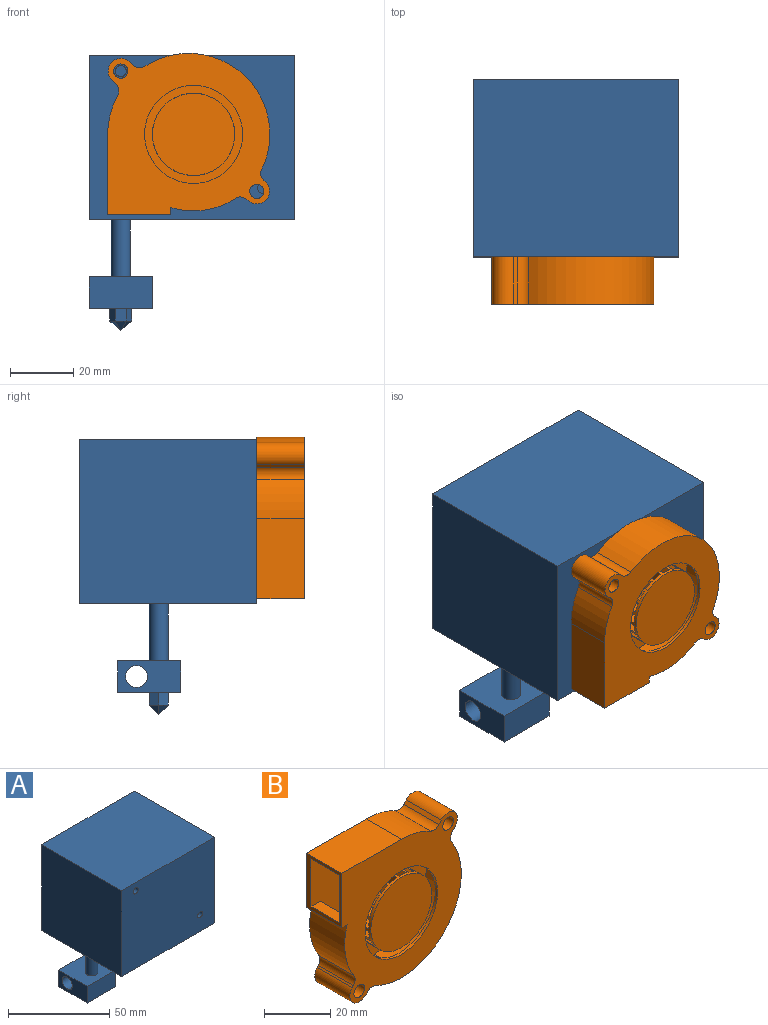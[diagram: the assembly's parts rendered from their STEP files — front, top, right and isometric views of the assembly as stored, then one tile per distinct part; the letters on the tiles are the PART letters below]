
ASSEMBLY  parts=2 mates=1
PART A: 30 faces, bbox 65x56x87 mm
  f0: cylinder r=3mm len=18mm, axis (0,0,-1), area 339.3mm2, adj f5,f25
  f1: plane 20x10mm, normal (1,0,0), area 161.5mm2, adj f2,f4,f5,f6,f7
  f2: plane 20x10mm, normal (0,1,0), area 200mm2, adj f1,f3,f5,f6
  f3: plane 20x10mm, normal (-1,0,0), area 161.5mm2, adj f2,f4,f5,f6,f7
  f4: plane 20x10mm, normal (0,-1,0), area 200mm2, adj f1,f3,f5,f6
  f5: plane 20x20mm, normal (0,0,1), area 371.7mm2, adj f0,f1,f2,f3,f4
  f6: plane 20x20mm, normal (0,0,-1), area 368.8mm2, adj f1,f2,f3,f4,f8,f9,f10,f11
  f7: cylinder r=3.5mm len=20mm, axis (1,0,0), area 439.8mm2, adj f1,f3
  f8: plane 4x3.46mm, normal (0,1,0), area 13.9mm2, adj f6,f9,f13,f14
  f9: plane 4x3mm, normal (0.87,0.5,0), area 13.9mm2, adj f6,f8,f10,f15
  f10: plane 4x3mm, normal (0.87,-0.5,0), area 13.9mm2, adj f6,f9,f11,f16
  f11: plane 4x3.46mm, normal (0,-1,0), area 13.9mm2, adj f6,f10,f12,f17
  f12: plane 4x3mm, normal (-0.87,-0.5,0), area 13.9mm2, adj f6,f11,f13,f18
  f13: plane 4x3mm, normal (-0.87,0.5,0), area 13.9mm2, adj f6,f8,f12,f19
  f14: plane 3.46x3mm, normal (0,0.71,-0.71), area 7.3mm2, adj f8,f15,f19
  f15: plane 3.46x3mm, normal (0.61,0.35,-0.71), area 7.3mm2, adj f9,f14,f16
  f16: plane 3.46x3mm, normal (0.61,-0.35,-0.71), area 7.3mm2, adj f10,f15,f17
  f17: plane 3.46x3mm, normal (0,-0.71,-0.71), area 7.3mm2, adj f11,f16,f18
  f18: plane 3.46x3mm, normal (-0.61,-0.35,-0.71), area 7.3mm2, adj f12,f17,f19
  f19: plane 3.46x3mm, normal (-0.61,0.35,-0.71), area 7.3mm2, adj f13,f14,f18
  f20: plane 56x52mm, normal (-1,0,0), area 2912mm2, adj f21,f23,f24,f25
  f21: plane 65x52mm, normal (0,-1,0), area 3360.8mm2, adj f20,f22,f24,f25,f26,f28
  f22: plane 56x52mm, normal (1,0,0), area 2912mm2, adj f21,f23,f24,f25
  f23: plane 65x52mm, normal (0,1,0), area 3380mm2, adj f20,f22,f24,f25
  f24: plane 65x56mm, normal (0,0,1), area 3640mm2, adj f20,f21,f22,f23
  f25: plane 65x56mm, normal (0,0,-1), area 3611.7mm2, adj f0,f20,f21,f22,f23
  f26: cylinder r=1.75mm len=25mm, axis (0,-1,0), area 274.9mm2, adj f21,f27
  f27: plane 3.5x3.5mm, normal (0,-1,0), area 9.6mm2, adj f26
  f28: cylinder r=1.75mm len=25mm, axis (0,-1,0), area 274.9mm2, adj f21,f29
  f29: plane 3.5x3.5mm, normal (0,-1,0), area 9.6mm2, adj f28
PART B: 132 faces, bbox 51x15x51.3 mm
  f0: plane 51.3x51mm, normal (0,-1,0), area 1490mm2, adj f1,f3,f4,f5,f6,f7,f8,f9
  f1: cylinder r=2.25mm len=15mm, axis (0,-1,0), area 212.1mm2, adj f0,f2
  f2: plane 51.3x51mm, normal (0,1,0), area 2244.8mm2, adj f1,f3,f4,f5,f6,f7,f8,f9
  f3: plane 20x15mm, normal (-1,0,0), area 85.3mm2, adj f0,f2,f14,f15,f16,f17,f25,f26
  f4: cylinder r=25.65mm len=15mm, axis (0,-1,0), area 194.4mm2, adj f0,f2,f15,f21
  f5: plane 15x1.06mm, normal (-0.75,0,0.66), area 21.3mm2, adj f0,f2,f6,f21
  f6: cylinder r=4mm len=15mm, axis (0,-1,0), area 188.5mm2, adj f0,f2,f5,f7
  f7: plane 15x1.36mm, normal (0.75,0,-0.66), area 27.2mm2, adj f0,f2,f6,f20
  f8: cylinder r=25.65mm len=39.47mm, axis (0,-1,0), area 798.2mm2, adj f0,f2,f9,f20
  f9: cylinder r=24.2mm len=15mm, axis (0,-1,0), area 196.5mm2, adj f0,f2,f8,f18
  f10: plane 15x0.45mm, normal (0.75,0,-0.66), area 9.1mm2, adj f0,f2,f11,f18
  f11: cylinder r=4mm len=15mm, axis (0,-1,0), area 188.5mm2, adj f0,f2,f10,f12
  f12: plane 15x0.54mm, normal (-0.75,0,0.66), area 10.8mm2, adj f0,f2,f11,f19
  f13: cylinder r=24.2mm len=20.34mm, axis (0,-1,0), area 318.2mm2, adj f0,f2,f14,f19
  f14: plane 15x2.27mm, normal (0,0,-1), area 34mm2, adj f0,f2,f3,f13
  f15: plane 25.35x15mm, normal (0,0,1), area 380.2mm2, adj f0,f2,f3,f4
  f16: plane 49.8x48.9mm, normal (0,-1,0), area 1831.8mm2, adj f3,f23,f24,f25,f26,f31
  f17: plane 49.8x48.9mm, normal (0,1,0), area 1231mm2, adj f3,f22,f23,f24,f25,f26
  f18: cylinder r=3mm len=15mm, axis (0,-1,0), area 59.3mm2, adj f0,f2,f9,f10
  f19: cylinder r=3mm len=15mm, axis (0,-1,0), area 58.6mm2, adj f0,f2,f12,f13
  f20: cylinder r=3mm len=15mm, axis (0,-1,0), area 58.3mm2, adj f0,f2,f7,f8
  f21: cylinder r=3mm len=15mm, axis (0,-1,0), area 60.8mm2, adj f0,f2,f4,f5
  f22: cylinder r=15.5mm len=31mm, axis (0,-1,0), area 97.4mm2, adj f0,f17
  f23: cylinder r=24.45mm len=48.84mm, axis (0,-1,0), area 916.9mm2, adj f16,f17,f24,f26
  f24: cylinder r=23mm len=31.3mm, axis (0,-1,0), area 564mm2, adj f16,f17,f23,f25
  f25: plane 12.2x3.95mm, normal (0,0,1), area 48.2mm2, adj f3,f16,f17,f24
  f26: plane 25.35x12.2mm, normal (0,0,-1), area 309.3mm2, adj f3,f16,f17,f23
  f27: cylinder r=2.25mm len=15mm, axis (0,-1,0), area 212.1mm2, adj f0,f2
  f28: cylinder r=13mm len=26mm, axis (0,-1,0), area 383.6mm2, adj f29,f30,f40,f41,f42,f43,f44,f45
  f29: plane 26x26mm, normal (0,-1,0), area 530.9mm2, adj f28
  f30: plane 6.3x3.02mm, normal (0,1,0), area 12.8mm2, adj f28,f37,f49,f50
  f31: cylinder r=7mm len=14mm, axis (0,-1,0), area 8.8mm2, adj f16,f94
  f32: cylinder r=7mm len=11mm, axis (0,-1,0), area 13.2mm2, adj f40,f79,f118,f123
  f33: cylinder r=7mm len=11mm, axis (0,-1,0), area 13.2mm2, adj f41,f42,f117,f124
  f34: cylinder r=7mm len=11mm, axis (0,-1,0), area 13.2mm2, adj f43,f44,f116,f125
  f35: cylinder r=7mm len=11mm, axis (0,-1,0), area 13.2mm2, adj f45,f46,f115,f126
  f36: cylinder r=7mm len=11mm, axis (0,-1,0), area 13.2mm2, adj f47,f48,f96,f113
  f37: cylinder r=7mm len=11mm, axis (0,-1,0), area 13.2mm2, adj f30,f49,f50,f114
  f38: cylinder r=7mm len=11mm, axis (0,-1,0), area 13.2mm2, adj f51,f52,f106,f128
  f39: cylinder r=7mm len=11mm, axis (0,-1,0), area 13.2mm2, adj f53,f54,f107,f129
  f40: plane 11x5.71mm, normal (0.95,0,0.31), area 66mm2, adj f28,f32,f118,f123
  f41: plane 11x5.74mm, normal (-0.95,0,-0.31), area 66.4mm2, adj f28,f33,f117,f124
  f42: plane 11x4.85mm, normal (0.81,0,0.59), area 66mm2, adj f28,f33,f117,f124
  f43: plane 11x4.88mm, normal (-0.81,0,-0.59), area 66.4mm2, adj f28,f34,f116,f125
  f44: plane 11x4.85mm, normal (0.59,0,0.81), area 66mm2, adj f28,f34,f116,f125
  f45: plane 11x4.88mm, normal (-0.59,0,-0.81), area 66.4mm2, adj f28,f35,f115,f126
  f46: plane 11x5.71mm, normal (0.31,0,0.95), area 66mm2, adj f28,f35,f115,f126
  f47: plane 11x5.74mm, normal (-0.31,0,-0.95), area 66.4mm2, adj f28,f36,f96,f113
  f48: plane 11x6mm, normal (0,0,1), area 66mm2, adj f28,f36,f96,f113
  f49: plane 11x6.03mm, normal (0,0,-1), area 66.4mm2, adj f28,f30,f37,f114
  f50: plane 11x5.71mm, normal (-0.31,0,0.95), area 66mm2, adj f28,f30,f37,f114
  f51: plane 11x5.74mm, normal (0.31,0,-0.95), area 66.4mm2, adj f28,f38,f106,f128
  f52: plane 11x4.85mm, normal (-0.59,0,0.81), area 66mm2, adj f28,f38,f106,f128
  f53: plane 11x4.88mm, normal (0.59,0,-0.81), area 66.4mm2, adj f28,f39,f107,f129
  f54: plane 11x4.85mm, normal (-0.81,0,0.59), area 66mm2, adj f28,f39,f107,f129
  f55: plane 11x4.88mm, normal (0.81,0,-0.59), area 66.4mm2, adj f28,f105,f108,f130
  f56: plane 11x5.71mm, normal (-0.95,0,0.31), area 66mm2, adj f28,f105,f108,f130
  f57: plane 11x5.74mm, normal (0.95,0,-0.31), area 66.4mm2, adj f28,f104,f109,f131
  f58: plane 11x6mm, normal (-1,0,0), area 66mm2, adj f28,f104,f109,f131
  f59: plane 11x6.03mm, normal (1,0,0), area 66.4mm2, adj f28,f100,f103,f110
  f60: plane 11x5.71mm, normal (-0.95,0,-0.31), area 66mm2, adj f28,f100,f103,f110
  f61: plane 11x5.74mm, normal (0.95,0,0.31), area 66.4mm2, adj f28,f99,f101,f111
  f62: plane 11x4.85mm, normal (-0.81,0,-0.59), area 66mm2, adj f28,f99,f101,f111
  f63: plane 11x4.88mm, normal (0.81,0,0.59), area 66.4mm2, adj f28,f98,f102,f112
  f64: plane 11x4.85mm, normal (-0.59,0,-0.81), area 66mm2, adj f28,f98,f102,f112
  f65: plane 11x4.88mm, normal (0.59,0,0.81), area 66.4mm2, adj f28,f86,f88,f97
  f66: plane 11x5.71mm, normal (-0.31,0,-0.95), area 66mm2, adj f28,f86,f88,f97
  f67: plane 11x5.74mm, normal (0.31,0,0.95), area 66.4mm2, adj f28,f85,f87,f95
  f68: plane 11x6mm, normal (0,0,-1), area 66mm2, adj f28,f85,f87,f95
  f69: plane 11x6.03mm, normal (0,0,1), area 66.4mm2, adj f28,f84,f89,f93
  f70: plane 11x5.71mm, normal (0.31,0,-0.95), area 66mm2, adj f28,f84,f89,f93
  f71: plane 11x5.74mm, normal (-0.31,0,0.95), area 66.4mm2, adj f28,f83,f90,f91
  f72: plane 11x4.85mm, normal (0.59,0,-0.81), area 66mm2, adj f28,f83,f90,f91
  f73: plane 11x4.88mm, normal (-0.59,0,0.81), area 66.4mm2, adj f28,f82,f92,f127
  f74: plane 11x4.85mm, normal (0.81,0,-0.59), area 66mm2, adj f28,f82,f92,f127
  f75: plane 11x4.88mm, normal (-0.81,0,0.59), area 66.4mm2, adj f28,f81,f120,f122
  f76: plane 11x5.71mm, normal (0.95,0,-0.31), area 66mm2, adj f28,f81,f120,f122
  f77: plane 11x5.74mm, normal (-0.95,0,0.31), area 66.4mm2, adj f28,f80,f119,f121
  f78: plane 11x6mm, normal (1,0,0), area 66mm2, adj f28,f80,f119,f121
  f79: plane 11x6.03mm, normal (-1,0,0), area 66.4mm2, adj f28,f32,f118,f123
  f80: cylinder r=7mm len=11mm, axis (0,-1,0), area 13.2mm2, adj f77,f78,f119,f121
  f81: cylinder r=7mm len=11mm, axis (0,-1,0), area 13.2mm2, adj f75,f76,f120,f122
  f82: cylinder r=7mm len=11mm, axis (0,-1,0), area 13.2mm2, adj f73,f74,f92,f127
  f83: cylinder r=7mm len=11mm, axis (0,-1,0), area 13.2mm2, adj f71,f72,f90,f91
  f84: cylinder r=7mm len=11mm, axis (0,-1,0), area 13.2mm2, adj f69,f70,f89,f93
  f85: cylinder r=7mm len=11mm, axis (0,-1,0), area 13.2mm2, adj f67,f68,f87,f95
  f86: cylinder r=7mm len=11mm, axis (0,-1,0), area 13.2mm2, adj f65,f66,f88,f97
  f87: plane 6.1x3.05mm, normal (0,1,0), area 12.8mm2, adj f28,f67,f68,f85
  f88: plane 6.17x4.65mm, normal (0,1,0), area 12.8mm2, adj f28,f65,f66,f86
  f89: plane 6.3x3.02mm, normal (0,1,0), area 12.8mm2, adj f28,f69,f70,f84
  f90: plane 6.36x4.55mm, normal (0,1,0), area 12.8mm2, adj f28,f71,f72,f83
  f91: plane 6.36x4.55mm, normal (0,-1,0), area 12.8mm2, adj f28,f71,f72,f83
  f92: plane 5.78x5.64mm, normal (0,-1,0), area 12.8mm2, adj f28,f73,f74,f82
  f93: plane 6.3x3.02mm, normal (0,-1,0), area 12.8mm2, adj f28,f69,f70,f84
  f94: plane 26x26mm, normal (0,1,0), area 377mm2, adj f28,f31
  f95: plane 6.1x3.05mm, normal (0,-1,0), area 12.8mm2, adj f28,f67,f68,f85
  f96: plane 6.1x3.05mm, normal (0,1,0), area 12.8mm2, adj f28,f36,f47,f48
  f97: plane 6.17x4.65mm, normal (0,-1,0), area 12.8mm2, adj f28,f65,f66,f86
  f98: plane 5.78x5.64mm, normal (0,-1,0), area 12.8mm2, adj f28,f63,f64,f102
  f99: plane 6.36x4.55mm, normal (0,-1,0), area 12.8mm2, adj f28,f61,f62,f101
  f100: plane 6.3x3.02mm, normal (0,-1,0), area 12.8mm2, adj f28,f59,f60,f103
  f101: cylinder r=7mm len=11mm, axis (0,-1,0), area 13.2mm2, adj f61,f62,f99,f111
  f102: cylinder r=7mm len=11mm, axis (0,-1,0), area 13.2mm2, adj f63,f64,f98,f112
  f103: cylinder r=7mm len=11mm, axis (0,-1,0), area 13.2mm2, adj f59,f60,f100,f110
  f104: cylinder r=7mm len=11mm, axis (0,-1,0), area 13.2mm2, adj f57,f58,f109,f131
  f105: cylinder r=7mm len=11mm, axis (0,-1,0), area 13.2mm2, adj f55,f56,f108,f130
  f106: plane 6.36x4.55mm, normal (0,1,0), area 12.8mm2, adj f28,f38,f51,f52
  f107: plane 5.78x5.64mm, normal (0,1,0), area 12.8mm2, adj f28,f39,f53,f54
  f108: plane 6.17x4.65mm, normal (0,1,0), area 12.8mm2, adj f28,f55,f56,f105
  f109: plane 6.1x3.05mm, normal (0,1,0), area 12.8mm2, adj f28,f57,f58,f104
  f110: plane 6.3x3.02mm, normal (0,1,0), area 12.8mm2, adj f28,f59,f60,f103
  f111: plane 6.36x4.55mm, normal (0,1,0), area 12.8mm2, adj f28,f61,f62,f101
  f112: plane 5.78x5.64mm, normal (0,1,0), area 12.8mm2, adj f28,f63,f64,f102
  f113: plane 6.1x3.05mm, normal (0,-1,0), area 12.8mm2, adj f28,f36,f47,f48
  f114: plane 6.3x3.02mm, normal (0,-1,0), area 12.8mm2, adj f28,f37,f49,f50
  f115: plane 6.17x4.65mm, normal (0,-1,0), area 12.8mm2, adj f28,f35,f45,f46
  f116: plane 5.78x5.64mm, normal (0,-1,0), area 12.8mm2, adj f28,f34,f43,f44
  f117: plane 6.36x4.55mm, normal (0,-1,0), area 12.8mm2, adj f28,f33,f41,f42
  f118: plane 6.3x3.02mm, normal (0,-1,0), area 12.8mm2, adj f28,f32,f40,f79
  f119: plane 6.1x3.05mm, normal (0,-1,0), area 12.8mm2, adj f28,f77,f78,f80
  f120: plane 6.17x4.65mm, normal (0,-1,0), area 12.8mm2, adj f28,f75,f76,f81
  f121: plane 6.1x3.05mm, normal (0,1,0), area 12.8mm2, adj f28,f77,f78,f80
  f122: plane 6.17x4.65mm, normal (0,1,0), area 12.8mm2, adj f28,f75,f76,f81
  f123: plane 6.3x3.02mm, normal (0,1,0), area 12.8mm2, adj f28,f32,f40,f79
  f124: plane 6.36x4.55mm, normal (0,1,0), area 12.8mm2, adj f28,f33,f41,f42
  f125: plane 5.78x5.64mm, normal (0,1,0), area 12.8mm2, adj f28,f34,f43,f44
  f126: plane 6.17x4.65mm, normal (0,1,0), area 12.8mm2, adj f28,f35,f45,f46
  f127: plane 5.78x5.64mm, normal (0,1,0), area 12.8mm2, adj f28,f73,f74,f82
  f128: plane 6.36x4.55mm, normal (0,-1,0), area 12.8mm2, adj f28,f38,f51,f52
  f129: plane 5.78x5.64mm, normal (0,-1,0), area 12.8mm2, adj f28,f39,f53,f54
  f130: plane 6.17x4.65mm, normal (0,-1,0), area 12.8mm2, adj f28,f55,f56,f105
  f131: plane 6.1x3.05mm, normal (0,-1,0), area 12.8mm2, adj f28,f57,f58,f104
PLACE A t=(-1.05,-46.9,-6.17)mm
PLACE B rot(axis=(0,-1,0),90deg) t=(21.95,-95.9,48.83)mm
MATE fastened A.f28 <-> B.f6  axis (0,-1,0) through (-1.05,-80.9,68.83)mm
